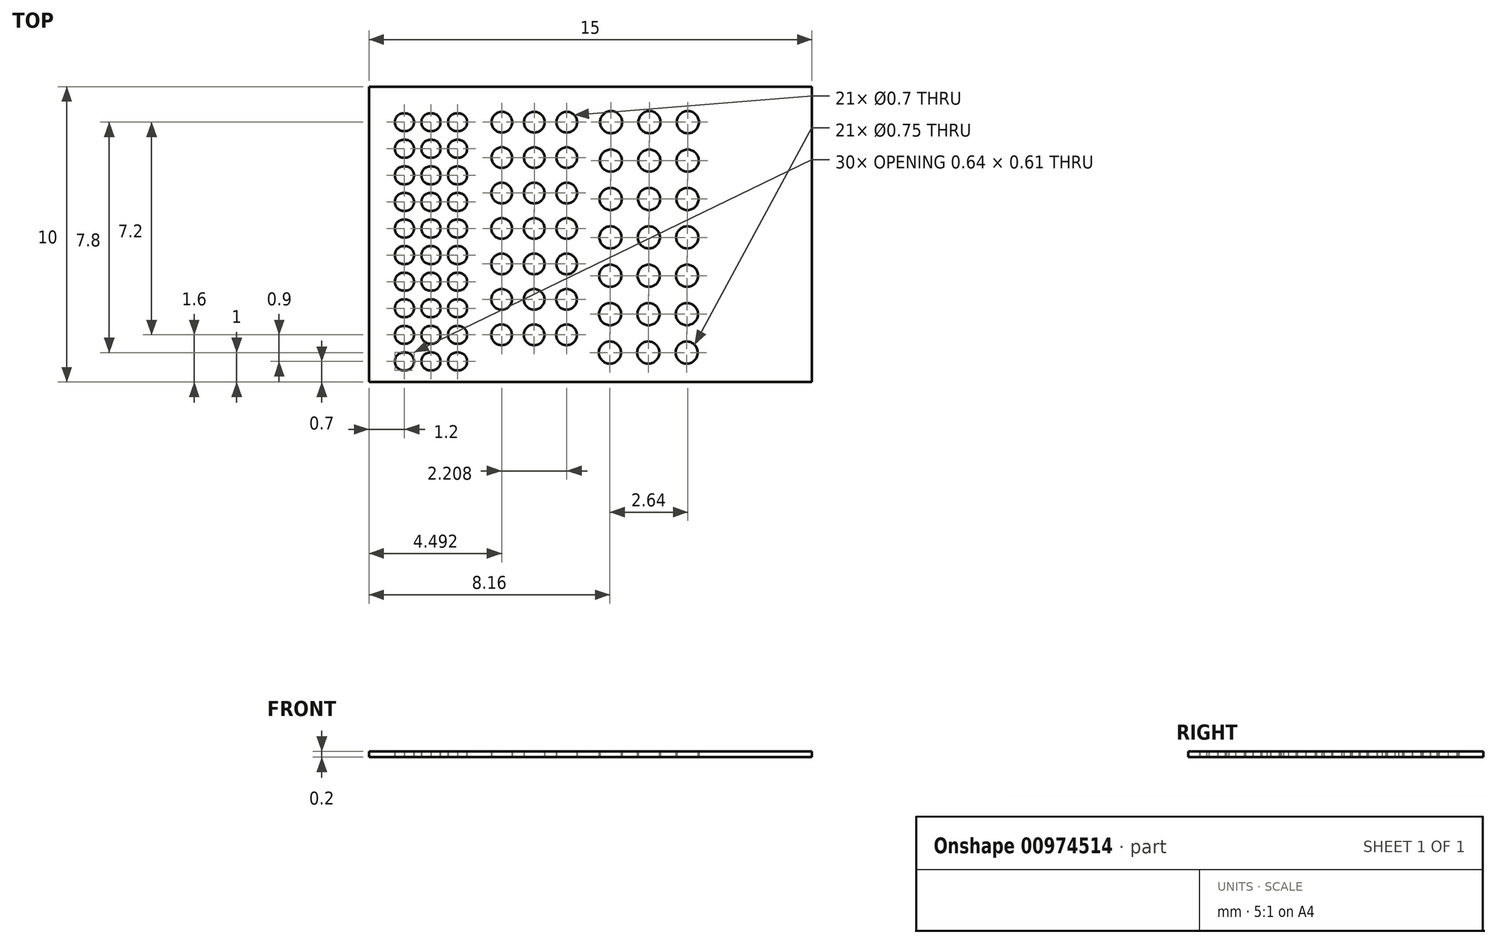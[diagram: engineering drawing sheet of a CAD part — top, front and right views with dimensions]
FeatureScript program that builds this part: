
annotation { "Feature Type Name" : "Feature", "Feature Type Description" : "" }
export const myFeature = defineFeature(function(context is Context, id is Id, definition is map)
    precondition{}
    {
        {
            var Q0;
            Q0=qCreatedBy(makeId("Top.planeOp"),FACE);
            var sketch = newSketch(context, id + "F0", { "sketchPlane" : qUnion([Q0])});
            skLineSegment(sketch, "E0.bottom", {"start": v(0, 0) * mm, "end": v(15, 0) * mm});
            skLineSegment(sketch, "E0.top", {"start": v(0, -10) * mm, "end": v(15, -10) * mm});
            skLineSegment(sketch, "E0.left", {"start": v(0, 0) * mm, "end": v(0, -10) * mm});
            skLineSegment(sketch, "E0.right", {"start": v(15, 0) * mm, "end": v(15, -10) * mm});
            skEllipse(sketch, "E1", {"center": v(1.2, -1.2) * mm, "majorRadius": 0.33 * mm, "minorRadius": 0.3 * mm, "majorAxis": v(0.93, 0.38)});
            skEllipse(sketch, "E2.1.0.0", {"center": v(2.1, -1.2) * mm, "majorRadius": 0.33 * mm, "minorRadius": 0.3 * mm, "majorAxis": v(0.93, 0.38)});
            skEllipse(sketch, "E2.2.0.0", {"center": v(3, -1.2) * mm, "majorRadius": 0.33 * mm, "minorRadius": 0.3 * mm, "majorAxis": v(0.93, 0.38)});
            skLineSegment(sketch, "E2.direction1", {"start": v(1.2, -1.2) * mm, "end": v(2.1, -1.2) * mm, "construction": true});
            skCircle(sketch, "E3", {"center": v(4.5, -1.2) * mm, "radius": 0.35 * mm});
            skCircle(sketch, "E4", {"center": v(8.2, -1.2) * mm, "radius": 0.38 * mm});
            skCircle(sketch, "E5.1.0.0", {"center": v(5.6, -1.2) * mm, "radius": 0.35 * mm});
            skCircle(sketch, "E5.2.0.0", {"center": v(6.7, -1.2) * mm, "radius": 0.35 * mm});
            skLineSegment(sketch, "E5.direction1", {"start": v(4.5, -1.2) * mm, "end": v(5.6, -1.2) * mm, "construction": true});
            skCircle(sketch, "E6.1.0.0", {"center": v(4.5, -2.4) * mm, "radius": 0.35 * mm});
            skLineSegment(sketch, "E6.1.0.1", {"start": v(4.5, -2.4) * mm, "end": v(5.6, -2.4) * mm, "construction": true});
            skCircle(sketch, "E6.1.0.2", {"center": v(5.6, -2.4) * mm, "radius": 0.35 * mm});
            skCircle(sketch, "E6.1.0.3", {"center": v(6.7, -2.4) * mm, "radius": 0.35 * mm});
            skCircle(sketch, "E6.2.0.0", {"center": v(4.5, -3.6) * mm, "radius": 0.35 * mm});
            skLineSegment(sketch, "E6.2.0.1", {"start": v(4.5, -3.6) * mm, "end": v(5.6, -3.6) * mm, "construction": true});
            skCircle(sketch, "E6.2.0.2", {"center": v(5.6, -3.6) * mm, "radius": 0.35 * mm});
            skCircle(sketch, "E6.2.0.3", {"center": v(6.7, -3.6) * mm, "radius": 0.35 * mm});
            skCircle(sketch, "E6.3.0.0", {"center": v(4.5, -4.8) * mm, "radius": 0.35 * mm});
            skLineSegment(sketch, "E6.3.0.1", {"start": v(4.5, -4.8) * mm, "end": v(5.6, -4.8) * mm, "construction": true});
            skCircle(sketch, "E6.3.0.2", {"center": v(5.6, -4.8) * mm, "radius": 0.35 * mm});
            skCircle(sketch, "E6.3.0.3", {"center": v(6.7, -4.8) * mm, "radius": 0.35 * mm});
            skCircle(sketch, "E6.4.0.0", {"center": v(4.5, -6) * mm, "radius": 0.35 * mm});
            skLineSegment(sketch, "E6.4.0.1", {"start": v(4.5, -6) * mm, "end": v(5.6, -6) * mm, "construction": true});
            skCircle(sketch, "E6.4.0.2", {"center": v(5.6, -6) * mm, "radius": 0.35 * mm});
            skCircle(sketch, "E6.4.0.3", {"center": v(6.7, -6) * mm, "radius": 0.35 * mm});
            skCircle(sketch, "E6.5.0.0", {"center": v(4.5, -7.2) * mm, "radius": 0.35 * mm});
            skLineSegment(sketch, "E6.5.0.1", {"start": v(4.5, -7.2) * mm, "end": v(5.6, -7.2) * mm, "construction": true});
            skCircle(sketch, "E6.5.0.2", {"center": v(5.6, -7.2) * mm, "radius": 0.35 * mm});
            skCircle(sketch, "E6.5.0.3", {"center": v(6.7, -7.2) * mm, "radius": 0.35 * mm});
            skCircle(sketch, "E6.6.0.0", {"center": v(4.5, -8.4) * mm, "radius": 0.35 * mm});
            skLineSegment(sketch, "E6.6.0.1", {"start": v(4.5, -8.4) * mm, "end": v(5.6, -8.4) * mm, "construction": true});
            skCircle(sketch, "E6.6.0.2", {"center": v(5.6, -8.4) * mm, "radius": 0.35 * mm});
            skCircle(sketch, "E6.6.0.3", {"center": v(6.7, -8.4) * mm, "radius": 0.35 * mm});
            skLineSegment(sketch, "E6.direction1", {"start": v(4.5, -1.2) * mm, "end": v(4.5, -2.4) * mm, "construction": true});
            skCircle(sketch, "E7.1.0.0", {"center": v(9.5, -1.2) * mm, "radius": 0.38 * mm});
            skCircle(sketch, "E7.2.0.0", {"center": v(10.8, -1.2) * mm, "radius": 0.38 * mm});
            skLineSegment(sketch, "E7.direction1", {"start": v(8.2, -1.2) * mm, "end": v(9.5, -1.2) * mm, "construction": true});
            skCircle(sketch, "E8.1.0.0", {"center": v(9.5, -2.5) * mm, "radius": 0.38 * mm});
            skCircle(sketch, "E8.1.0.1", {"center": v(10.8, -2.5) * mm, "radius": 0.38 * mm});
            skCircle(sketch, "E8.1.0.2", {"center": v(8.2, -2.5) * mm, "radius": 0.38 * mm});
            skLineSegment(sketch, "E8.1.0.3", {"start": v(8.2, -2.5) * mm, "end": v(9.5, -2.5) * mm, "construction": true});
            skCircle(sketch, "E8.2.0.0", {"center": v(9.49, -3.8) * mm, "radius": 0.38 * mm});
            skCircle(sketch, "E8.2.0.1", {"center": v(10.79, -3.8) * mm, "radius": 0.38 * mm});
            skCircle(sketch, "E8.2.0.2", {"center": v(8.19, -3.8) * mm, "radius": 0.38 * mm});
            skLineSegment(sketch, "E8.2.0.3", {"start": v(8.19, -3.8) * mm, "end": v(9.49, -3.8) * mm, "construction": true});
            skCircle(sketch, "E8.3.0.0", {"center": v(9.48, -5.1) * mm, "radius": 0.38 * mm});
            skCircle(sketch, "E8.3.0.1", {"center": v(10.78, -5.1) * mm, "radius": 0.38 * mm});
            skCircle(sketch, "E8.3.0.2", {"center": v(8.18, -5.1) * mm, "radius": 0.38 * mm});
            skLineSegment(sketch, "E8.3.0.3", {"start": v(8.18, -5.1) * mm, "end": v(9.48, -5.1) * mm, "construction": true});
            skCircle(sketch, "E8.4.0.0", {"center": v(9.47, -6.4) * mm, "radius": 0.38 * mm});
            skCircle(sketch, "E8.4.0.1", {"center": v(10.77, -6.4) * mm, "radius": 0.38 * mm});
            skCircle(sketch, "E8.4.0.2", {"center": v(8.17, -6.4) * mm, "radius": 0.38 * mm});
            skLineSegment(sketch, "E8.4.0.3", {"start": v(8.17, -6.4) * mm, "end": v(9.47, -6.4) * mm, "construction": true});
            skCircle(sketch, "E8.5.0.0", {"center": v(9.47, -7.7) * mm, "radius": 0.38 * mm});
            skCircle(sketch, "E8.5.0.1", {"center": v(10.77, -7.7) * mm, "radius": 0.38 * mm});
            skCircle(sketch, "E8.5.0.2", {"center": v(8.17, -7.7) * mm, "radius": 0.38 * mm});
            skLineSegment(sketch, "E8.5.0.3", {"start": v(8.17, -7.7) * mm, "end": v(9.47, -7.7) * mm, "construction": true});
            skCircle(sketch, "E8.6.0.0", {"center": v(9.46, -9) * mm, "radius": 0.38 * mm});
            skCircle(sketch, "E8.6.0.1", {"center": v(10.76, -9) * mm, "radius": 0.38 * mm});
            skCircle(sketch, "E8.6.0.2", {"center": v(8.16, -9) * mm, "radius": 0.38 * mm});
            skLineSegment(sketch, "E8.6.0.3", {"start": v(8.16, -9) * mm, "end": v(9.46, -9) * mm, "construction": true});
            skLineSegment(sketch, "E8.direction1", {"start": v(8.2, -1.2) * mm, "end": v(8.2, -2.5) * mm, "construction": true});
            skEllipse(sketch, "E9.MirrorC", {"center": v(2.1, -1.2) * mm, "majorRadius": 0.33 * mm, "minorRadius": 0.3 * mm, "majorAxis": v(0.93, -0.38)});
            skEllipse(sketch, "E10.MirrorC", {"center": v(1.2, -1.2) * mm, "majorRadius": 0.33 * mm, "minorRadius": 0.3 * mm, "majorAxis": v(0.93, -0.38)});
            skEllipse(sketch, "E11.MirrorC", {"center": v(3, -1.2) * mm, "majorRadius": 0.33 * mm, "minorRadius": 0.3 * mm, "majorAxis": v(0.93, -0.38)});
            skEllipse(sketch, "E12.1.0.0", {"center": v(2.1, -2.1) * mm, "majorRadius": 0.33 * mm, "minorRadius": 0.3 * mm, "majorAxis": v(0.93, 0.38)});
            skEllipse(sketch, "E12.1.0.1", {"center": v(1.2, -2.1) * mm, "majorRadius": 0.33 * mm, "minorRadius": 0.3 * mm, "majorAxis": v(0.93, -0.38)});
            skEllipse(sketch, "E12.1.0.2", {"center": v(3, -2.1) * mm, "majorRadius": 0.33 * mm, "minorRadius": 0.3 * mm, "majorAxis": v(0.93, 0.38)});
            skLineSegment(sketch, "E12.1.0.3", {"start": v(1.2, -2.1) * mm, "end": v(2.1, -2.1) * mm, "construction": true});
            skEllipse(sketch, "E12.1.0.4", {"center": v(1.2, -2.1) * mm, "majorRadius": 0.33 * mm, "minorRadius": 0.3 * mm, "majorAxis": v(0.93, 0.38)});
            skEllipse(sketch, "E12.1.0.5", {"center": v(3, -2.1) * mm, "majorRadius": 0.33 * mm, "minorRadius": 0.3 * mm, "majorAxis": v(0.93, -0.38)});
            skEllipse(sketch, "E12.1.0.6", {"center": v(2.1, -2.1) * mm, "majorRadius": 0.33 * mm, "minorRadius": 0.3 * mm, "majorAxis": v(0.93, -0.38)});
            skEllipse(sketch, "E12.2.0.0", {"center": v(2.1, -3) * mm, "majorRadius": 0.33 * mm, "minorRadius": 0.3 * mm, "majorAxis": v(0.93, 0.38)});
            skEllipse(sketch, "E12.2.0.1", {"center": v(1.2, -3) * mm, "majorRadius": 0.33 * mm, "minorRadius": 0.3 * mm, "majorAxis": v(0.93, -0.38)});
            skEllipse(sketch, "E12.2.0.2", {"center": v(3, -3) * mm, "majorRadius": 0.33 * mm, "minorRadius": 0.3 * mm, "majorAxis": v(0.93, 0.38)});
            skLineSegment(sketch, "E12.2.0.3", {"start": v(1.2, -3) * mm, "end": v(2.1, -3) * mm, "construction": true});
            skEllipse(sketch, "E12.2.0.4", {"center": v(1.2, -3) * mm, "majorRadius": 0.33 * mm, "minorRadius": 0.3 * mm, "majorAxis": v(0.93, 0.38)});
            skEllipse(sketch, "E12.2.0.5", {"center": v(3, -3) * mm, "majorRadius": 0.33 * mm, "minorRadius": 0.3 * mm, "majorAxis": v(0.93, -0.38)});
            skEllipse(sketch, "E12.2.0.6", {"center": v(2.1, -3) * mm, "majorRadius": 0.33 * mm, "minorRadius": 0.3 * mm, "majorAxis": v(0.93, -0.38)});
            skEllipse(sketch, "E12.3.0.0", {"center": v(2.1, -3.9) * mm, "majorRadius": 0.33 * mm, "minorRadius": 0.3 * mm, "majorAxis": v(0.93, 0.38)});
            skEllipse(sketch, "E12.3.0.1", {"center": v(1.2, -3.9) * mm, "majorRadius": 0.33 * mm, "minorRadius": 0.3 * mm, "majorAxis": v(0.93, -0.38)});
            skEllipse(sketch, "E12.3.0.2", {"center": v(3, -3.9) * mm, "majorRadius": 0.33 * mm, "minorRadius": 0.3 * mm, "majorAxis": v(0.93, 0.38)});
            skLineSegment(sketch, "E12.3.0.3", {"start": v(1.2, -3.9) * mm, "end": v(2.1, -3.9) * mm, "construction": true});
            skEllipse(sketch, "E12.3.0.4", {"center": v(1.2, -3.9) * mm, "majorRadius": 0.33 * mm, "minorRadius": 0.3 * mm, "majorAxis": v(0.93, 0.38)});
            skEllipse(sketch, "E12.3.0.5", {"center": v(3, -3.9) * mm, "majorRadius": 0.33 * mm, "minorRadius": 0.3 * mm, "majorAxis": v(0.93, -0.38)});
            skEllipse(sketch, "E12.3.0.6", {"center": v(2.1, -3.9) * mm, "majorRadius": 0.33 * mm, "minorRadius": 0.3 * mm, "majorAxis": v(0.93, -0.38)});
            skEllipse(sketch, "E12.4.0.0", {"center": v(2.1, -4.8) * mm, "majorRadius": 0.33 * mm, "minorRadius": 0.3 * mm, "majorAxis": v(0.93, 0.38)});
            skEllipse(sketch, "E12.4.0.1", {"center": v(1.2, -4.8) * mm, "majorRadius": 0.33 * mm, "minorRadius": 0.3 * mm, "majorAxis": v(0.93, -0.38)});
            skEllipse(sketch, "E12.4.0.2", {"center": v(3, -4.8) * mm, "majorRadius": 0.33 * mm, "minorRadius": 0.3 * mm, "majorAxis": v(0.93, 0.38)});
            skLineSegment(sketch, "E12.4.0.3", {"start": v(1.2, -4.8) * mm, "end": v(2.1, -4.8) * mm, "construction": true});
            skEllipse(sketch, "E12.4.0.4", {"center": v(1.2, -4.8) * mm, "majorRadius": 0.33 * mm, "minorRadius": 0.3 * mm, "majorAxis": v(0.93, 0.38)});
            skEllipse(sketch, "E12.4.0.5", {"center": v(3, -4.8) * mm, "majorRadius": 0.33 * mm, "minorRadius": 0.3 * mm, "majorAxis": v(0.93, -0.38)});
            skEllipse(sketch, "E12.4.0.6", {"center": v(2.1, -4.8) * mm, "majorRadius": 0.33 * mm, "minorRadius": 0.3 * mm, "majorAxis": v(0.93, -0.38)});
            skEllipse(sketch, "E12.5.0.0", {"center": v(2.1, -5.7) * mm, "majorRadius": 0.33 * mm, "minorRadius": 0.3 * mm, "majorAxis": v(0.93, 0.38)});
            skEllipse(sketch, "E12.5.0.1", {"center": v(1.2, -5.7) * mm, "majorRadius": 0.33 * mm, "minorRadius": 0.3 * mm, "majorAxis": v(0.93, -0.38)});
            skEllipse(sketch, "E12.5.0.2", {"center": v(3, -5.7) * mm, "majorRadius": 0.33 * mm, "minorRadius": 0.3 * mm, "majorAxis": v(0.93, 0.38)});
            skLineSegment(sketch, "E12.5.0.3", {"start": v(1.2, -5.7) * mm, "end": v(2.1, -5.7) * mm, "construction": true});
            skEllipse(sketch, "E12.5.0.4", {"center": v(1.2, -5.7) * mm, "majorRadius": 0.33 * mm, "minorRadius": 0.3 * mm, "majorAxis": v(0.93, 0.38)});
            skEllipse(sketch, "E12.5.0.5", {"center": v(3, -5.7) * mm, "majorRadius": 0.33 * mm, "minorRadius": 0.3 * mm, "majorAxis": v(0.93, -0.38)});
            skEllipse(sketch, "E12.5.0.6", {"center": v(2.1, -5.7) * mm, "majorRadius": 0.33 * mm, "minorRadius": 0.3 * mm, "majorAxis": v(0.93, -0.38)});
            skEllipse(sketch, "E12.6.0.0", {"center": v(2.1, -6.6) * mm, "majorRadius": 0.33 * mm, "minorRadius": 0.3 * mm, "majorAxis": v(0.93, 0.38)});
            skEllipse(sketch, "E12.6.0.1", {"center": v(1.2, -6.6) * mm, "majorRadius": 0.33 * mm, "minorRadius": 0.3 * mm, "majorAxis": v(0.93, -0.38)});
            skEllipse(sketch, "E12.6.0.2", {"center": v(3, -6.6) * mm, "majorRadius": 0.33 * mm, "minorRadius": 0.3 * mm, "majorAxis": v(0.93, 0.38)});
            skLineSegment(sketch, "E12.6.0.3", {"start": v(1.2, -6.6) * mm, "end": v(2.1, -6.6) * mm, "construction": true});
            skEllipse(sketch, "E12.6.0.4", {"center": v(1.2, -6.6) * mm, "majorRadius": 0.33 * mm, "minorRadius": 0.3 * mm, "majorAxis": v(0.93, 0.38)});
            skEllipse(sketch, "E12.6.0.5", {"center": v(3, -6.6) * mm, "majorRadius": 0.33 * mm, "minorRadius": 0.3 * mm, "majorAxis": v(0.93, -0.38)});
            skEllipse(sketch, "E12.6.0.6", {"center": v(2.1, -6.6) * mm, "majorRadius": 0.33 * mm, "minorRadius": 0.3 * mm, "majorAxis": v(0.93, -0.38)});
            skEllipse(sketch, "E12.7.0.0", {"center": v(2.1, -7.5) * mm, "majorRadius": 0.33 * mm, "minorRadius": 0.3 * mm, "majorAxis": v(0.93, 0.38)});
            skEllipse(sketch, "E12.7.0.1", {"center": v(1.2, -7.5) * mm, "majorRadius": 0.33 * mm, "minorRadius": 0.3 * mm, "majorAxis": v(0.93, -0.38)});
            skEllipse(sketch, "E12.7.0.2", {"center": v(3, -7.5) * mm, "majorRadius": 0.33 * mm, "minorRadius": 0.3 * mm, "majorAxis": v(0.93, 0.38)});
            skLineSegment(sketch, "E12.7.0.3", {"start": v(1.2, -7.5) * mm, "end": v(2.1, -7.5) * mm, "construction": true});
            skEllipse(sketch, "E12.7.0.4", {"center": v(1.2, -7.5) * mm, "majorRadius": 0.33 * mm, "minorRadius": 0.3 * mm, "majorAxis": v(0.93, 0.38)});
            skEllipse(sketch, "E12.7.0.5", {"center": v(3, -7.5) * mm, "majorRadius": 0.33 * mm, "minorRadius": 0.3 * mm, "majorAxis": v(0.93, -0.38)});
            skEllipse(sketch, "E12.7.0.6", {"center": v(2.1, -7.5) * mm, "majorRadius": 0.33 * mm, "minorRadius": 0.3 * mm, "majorAxis": v(0.93, -0.38)});
            skEllipse(sketch, "E12.8.0.0", {"center": v(2.1, -8.4) * mm, "majorRadius": 0.33 * mm, "minorRadius": 0.3 * mm, "majorAxis": v(0.93, 0.38)});
            skEllipse(sketch, "E12.8.0.1", {"center": v(1.2, -8.4) * mm, "majorRadius": 0.33 * mm, "minorRadius": 0.3 * mm, "majorAxis": v(0.93, -0.38)});
            skEllipse(sketch, "E12.8.0.2", {"center": v(3, -8.4) * mm, "majorRadius": 0.33 * mm, "minorRadius": 0.3 * mm, "majorAxis": v(0.93, 0.38)});
            skLineSegment(sketch, "E12.8.0.3", {"start": v(1.2, -8.4) * mm, "end": v(2.1, -8.4) * mm, "construction": true});
            skEllipse(sketch, "E12.8.0.4", {"center": v(1.2, -8.4) * mm, "majorRadius": 0.33 * mm, "minorRadius": 0.3 * mm, "majorAxis": v(0.93, 0.38)});
            skEllipse(sketch, "E12.8.0.5", {"center": v(3, -8.4) * mm, "majorRadius": 0.33 * mm, "minorRadius": 0.3 * mm, "majorAxis": v(0.93, -0.38)});
            skEllipse(sketch, "E12.8.0.6", {"center": v(2.1, -8.4) * mm, "majorRadius": 0.33 * mm, "minorRadius": 0.3 * mm, "majorAxis": v(0.93, -0.38)});
            skLineSegment(sketch, "E12.direction1", {"start": v(1.2, -1.2) * mm, "end": v(1.2, -2.1) * mm, "construction": true});
            skEllipse(sketch, "E13.0.9.0", {"center": v(2.1, -9.3) * mm, "majorRadius": 0.33 * mm, "minorRadius": 0.3 * mm, "majorAxis": v(0.93, 0.38)});
            skEllipse(sketch, "E13.2.9.0", {"center": v(1.2, -9.3) * mm, "majorRadius": 0.33 * mm, "minorRadius": 0.3 * mm, "majorAxis": v(0.93, -0.38)});
            skEllipse(sketch, "E13.4.9.0", {"center": v(3, -9.3) * mm, "majorRadius": 0.33 * mm, "minorRadius": 0.3 * mm, "majorAxis": v(0.93, 0.38)});
            skLineSegment(sketch, "E13.6.9.0", {"start": v(1.2, -9.3) * mm, "end": v(2.1, -9.3) * mm, "construction": true});
            skEllipse(sketch, "E13.9.9.0", {"center": v(1.2, -9.3) * mm, "majorRadius": 0.33 * mm, "minorRadius": 0.3 * mm, "majorAxis": v(0.93, 0.38)});
            skEllipse(sketch, "E13.11.9.0", {"center": v(3, -9.3) * mm, "majorRadius": 0.33 * mm, "minorRadius": 0.3 * mm, "majorAxis": v(0.93, -0.38)});
            skEllipse(sketch, "E13.13.9.0", {"center": v(2.1, -9.3) * mm, "majorRadius": 0.33 * mm, "minorRadius": 0.3 * mm, "majorAxis": v(0.93, -0.38)});
            skSolve(sketch);
        }
        {
            var Q0;
            Q0=makeQuery(id+"F0.imprint","IMPRINT",FACE,{"disambiguationData":[TD([[makeQuery(id+"F0.imprint","IMPRINT",EDGE,{"derivedFrom":sQuery(id+"F0.wireOp",EDGE,"E0.bottom")}),-1.0]])]});
            extrude(context, id + "F1", {"entities" : qUnion([Q0]), "depth" : 0.2 * mm, "offsetDistance" : 25.4 * mm});
        }
    });
